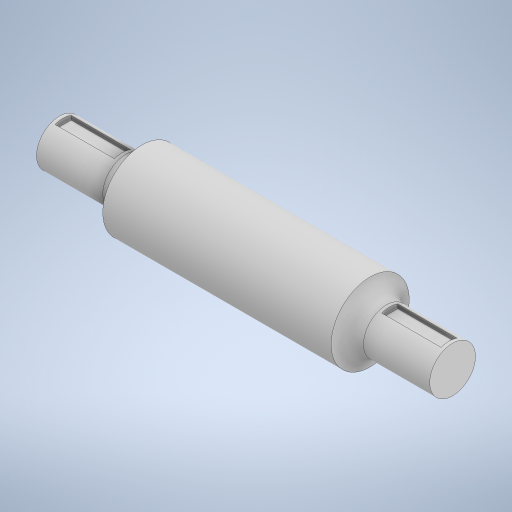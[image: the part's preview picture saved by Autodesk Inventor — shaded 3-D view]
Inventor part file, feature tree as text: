
AUTODESK INVENTOR PART (.ipt)
format: ipt  version: 2024 (Build 280153000, 153)  size: 290,816 bytes
history: native  units: mm
features: sketch x2, revolve x1, plane x1, extrude x1
ambient origin geometry x8: Origin, YZ Plane, XZ Plane, XY Plane, X Axis, Y Axis, Z Axis, Center Point
bodies: Solid1 (feature_tree)
feature tree (5):
  revolve  "Revolution1"  [1 undecoded]
  plane  "Work Plane1"
  extrude  "Extrusion1"  Depth=26.0mm
  sketch  "Sketch1"  dims[d5=360.0deg d8=26.0mm]
  sketch  "Sketch3"  dims[d9=7.0mm d10=26.0mm d11=7.0mm d12=2.4mm d13=0.0mm]
note: 1 required parameter value undecoded (feature->parameter linkage not recoverable at this tier; creation-order binding heuristic only, values carry confidence <= 0.55)
